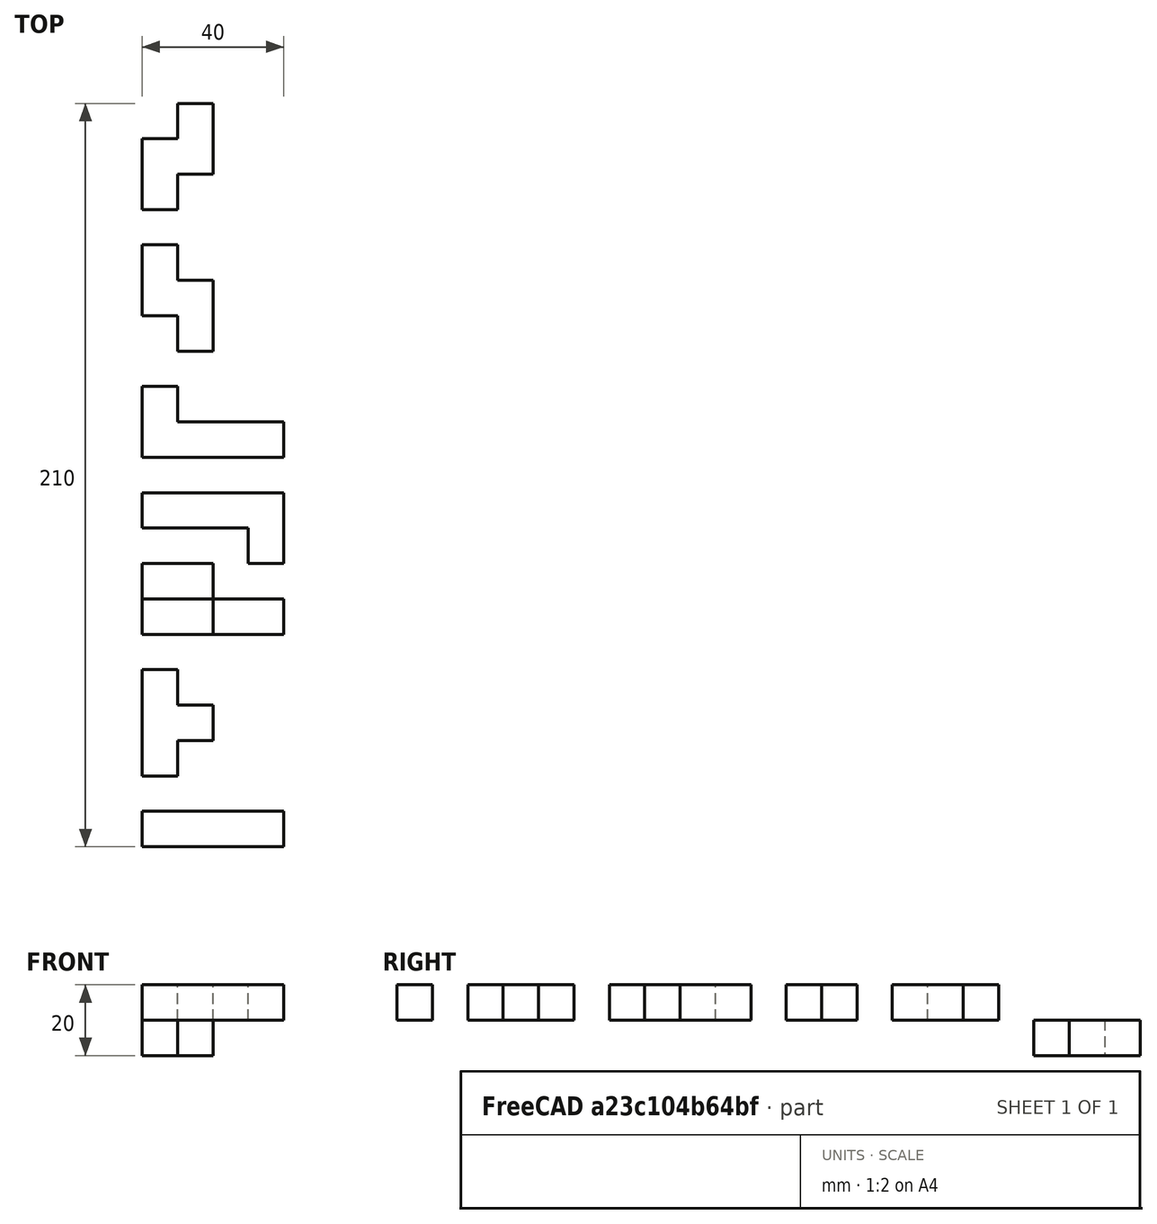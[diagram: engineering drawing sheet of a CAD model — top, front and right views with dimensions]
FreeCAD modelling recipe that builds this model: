
FCSTD DOCUMENT  (FreeCAD 0.18.4R)
Label: tutorial_freecad_ex05_B
License: All rights reserved
LicenseURL: http://en.wikipedia.org/wiki/All_rights_reserved
objects: Part::Box×30, Part::MultiFuse×7, Part::Feature×2
note: 39 computed .brp shape members not serialized (recipe doc carries the construction recipe); baked Part::Feature solids carry a one-line shape summary decoded from their .brp

FEATURE [Part::Box] Box  label="Cubo"
  AttacherType = Attacher::AttachEngine3D
  Height = 10
  Length = 10
  Width = 10
FEATURE [Part::Box] Box001  label="Cubo001"
  AttacherType = Attacher::AttachEngine3D
  Height = 10
  Length = 10
  Placement = pos=(10,0,0) rot=(0,0,1;0rad)
  Width = 10
FEATURE [Part::Box] Box002  label="Cubo002"
  AttacherType = Attacher::AttachEngine3D
  Height = 10
  Length = 10
  Placement = pos=(20,0,0) rot=(0,0,1;0rad)
  Width = 10
FEATURE [Part::Box] Box003  label="Cubo003"
  AttacherType = Attacher::AttachEngine3D
  Height = 10
  Length = 10
  Placement = pos=(30,0,0) rot=(0,0,1;0rad)
  Width = 10
FEATURE [Part::MultiFuse] Fusion
  Placement = pos=(0,-100,0) rot=(0,0,1;0rad)
  Refine = true
  Shapes = -> [Box003,Box,Box001,Box002]
FEATURE [Part::Feature] Fusion001
  Placement = pos=(0,-40,0) rot=(0,0,1;0rad)
  shape: bbox 40 x 10 x 10 mm, 6 faces (baked)
FEATURE [Part::Box] Box004  label="Cubo004"
  AttacherType = Attacher::AttachEngine3D
  Height = 10
  Length = 10
  Width = 10
FEATURE [Part::Box] Box005  label="Cubo005"
  AttacherType = Attacher::AttachEngine3D
  Height = 10
  Length = 10
  Placement = pos=(0,10,0) rot=(0,0,1;0rad)
  Width = 10
FEATURE [Part::Box] Box006  label="Cubo006"
  AttacherType = Attacher::AttachEngine3D
  Height = 10
  Length = 10
  Placement = pos=(0,20,0) rot=(0,0,1;0rad)
  Width = 10
FEATURE [Part::Box] Box007  label="Cubo007"
  AttacherType = Attacher::AttachEngine3D
  Height = 10
  Length = 10
  Placement = pos=(10,10,0) rot=(0,0,1;0rad)
  Width = 10
FEATURE [Part::MultiFuse] Fusion002
  Placement = pos=(0,-80,0) rot=(0,0,1;0rad)
  Refine = true
  Shapes = -> [Box004,Box005,Box007,Box006]
FEATURE [Part::Feature] Fusion002001  label="Fusion003"
  Placement = pos=(0,-80,0) rot=(0,0,1;0rad)
  shape: bbox 20 x 30 x 10 mm, 10 faces (baked)
FEATURE [Part::Box] Box008  label="Cubo008"
  AttacherType = Attacher::AttachEngine3D
  Height = 10
  Length = 10
  Width = 10
FEATURE [Part::Box] Box009  label="Cubo009"
  AttacherType = Attacher::AttachEngine3D
  Height = 10
  Length = 10
  Placement = pos=(0,10,0) rot=(0,0,1;0rad)
  Width = 10
FEATURE [Part::Box] Box010  label="Cubo010"
  AttacherType = Attacher::AttachEngine3D
  Height = 10
  Length = 10
  Placement = pos=(10,0,0) rot=(0,0,1;0rad)
  Width = 10
FEATURE [Part::Box] Box011  label="Cubo011"
  AttacherType = Attacher::AttachEngine3D
  Height = 10
  Length = 10
  Placement = pos=(10,10,0) rot=(0,0,1;0rad)
  Width = 10
FEATURE [Part::MultiFuse] Fusion002002
  Placement = pos=(0,-40,0) rot=(0,0,1;0rad)
  Refine = true
  Shapes = -> [Box008,Box011,Box009,Box010]
FEATURE [Part::Box] Box012  label="Cubo012"
  AttacherType = Attacher::AttachEngine3D
  Height = 10
  Length = 10
  Width = 10
FEATURE [Part::Box] Box013  label="Cubo013"
  AttacherType = Attacher::AttachEngine3D
  Height = 10
  Length = 10
  Placement = pos=(10,0,0) rot=(0,0,1;0rad)
  Width = 10
FEATURE [Part::Box] Box014  label="Cubo014"
  AttacherType = Attacher::AttachEngine3D
  Height = 10
  Length = 10
  Placement = pos=(20,0,0) rot=(0,0,1;0rad)
  Width = 10
FEATURE [Part::Box] Box015  label="Cubo015"
  AttacherType = Attacher::AttachEngine3D
  Height = 10
  Length = 10
  Placement = pos=(30,0,0) rot=(0,0,1;0rad)
  Width = 10
FEATURE [Part::Box] Box016  label="Cubo016"
  AttacherType = Attacher::AttachEngine3D
  Height = 10
  Length = 10
  Placement = pos=(0,10,0) rot=(0,0,1;0rad)
  Width = 10
FEATURE [Part::MultiFuse] Fusion002003
  Placement = pos=(0,10,0) rot=(0,0,1;0rad)
  Refine = true
  Shapes = -> [Box012,Box015,Box013,Box014,Box016]
FEATURE [Part::Box] Box017  label="Cubo017"
  AttacherType = Attacher::AttachEngine3D
  Height = 10
  Length = 10
  Placement = pos=(30,0,0) rot=(0,0,1;0rad)
  Width = 10
FEATURE [Part::Box] Box018  label="Cubo018"
  AttacherType = Attacher::AttachEngine3D
  Height = 10
  Length = 10
  Placement = pos=(10,0,0) rot=(0,0,1;0rad)
  Width = 10
FEATURE [Part::Box] Box019  label="Cubo019"
  AttacherType = Attacher::AttachEngine3D
  Height = 10
  Length = 10
  Placement = pos=(20,0,0) rot=(0,0,1;0rad)
  Width = 10
FEATURE [Part::Box] Box020  label="Cubo020"
  AttacherType = Attacher::AttachEngine3D
  Height = 10
  Length = 10
  Width = 10
FEATURE [Part::Box] Box021  label="Cubo021"
  AttacherType = Attacher::AttachEngine3D
  Height = 10
  Length = 10
  Placement = pos=(0,10,0) rot=(0,0,1;0rad)
  Width = 10
FEATURE [Part::MultiFuse] Fusion002004
  Placement = pos=(40,0,0) rot=(0,0,1;3.14159rad)
  Refine = true
  Shapes = -> [Box020,Box017,Box018,Box019,Box021]
  expr: Placement.Rotation.Angle = 180
FEATURE [Part::Box] Box022  label="Cubo022"
  AttacherType = Attacher::AttachEngine3D
  Height = 10
  Length = 10
  Placement = pos=(10,0,0) rot=(0,0,1;0rad)
  Width = 10
  expr: Placement.Rotation.Axis.z = 0
FEATURE [Part::Box] Box023  label="Cubo023"
  AttacherType = Attacher::AttachEngine3D
  Height = 10
  Length = 10
  Placement = pos=(10,10,0) rot=(0,0,1;0rad)
  Width = 10
FEATURE [Part::Box] Box024  label="Cubo024"
  AttacherType = Attacher::AttachEngine3D
  Height = 10
  Length = 10
  Placement = pos=(0,10,0) rot=(0,0,1;0rad)
  Width = 10
FEATURE [Part::Box] Box025  label="Cubo025"
  AttacherType = Attacher::AttachEngine3D
  Height = 10
  Length = 10
  Placement = pos=(0,20,0) rot=(0,0,1;0rad)
  Width = 10
FEATURE [Part::MultiFuse] Fusion002005
  Placement = pos=(0,40,0) rot=(0,0,1;0rad)
  Refine = true
  Shapes = -> [Box022,Box024,Box023,Box025]
FEATURE [Part::Box] Box026  label="Cubo026"
  AttacherType = Attacher::AttachEngine3D
  Height = 10
  Length = 10
  Placement = pos=(0,10,0) rot=(0,0,1;0rad)
  Width = 10
FEATURE [Part::Box] Box027  label="Cubo027"
  AttacherType = Attacher::AttachEngine3D
  Height = 10
  Length = 10
  Placement = pos=(10,10,0) rot=(0,0,1;0rad)
  Width = 10
FEATURE [Part::Box] Box028  label="Cubo028"
  AttacherType = Attacher::AttachEngine3D
  Height = 10
  Length = 10
  Placement = pos=(0,20,0) rot=(0,0,1;0rad)
  Width = 10
FEATURE [Part::Box] Box029  label="Cubo029"
  AttacherType = Attacher::AttachEngine3D
  Height = 10
  Length = 10
  Placement = pos=(10,0,0) rot=(0,0,1;0rad)
  Width = 10
  expr: Placement.Rotation.Axis.z = 0
FEATURE [Part::MultiFuse] Fusion002006
  Placement = pos=(20,80,0) rot=(0,1,0;3.14159rad)
  Refine = true
  Shapes = -> [Box029,Box026,Box027,Box028]
